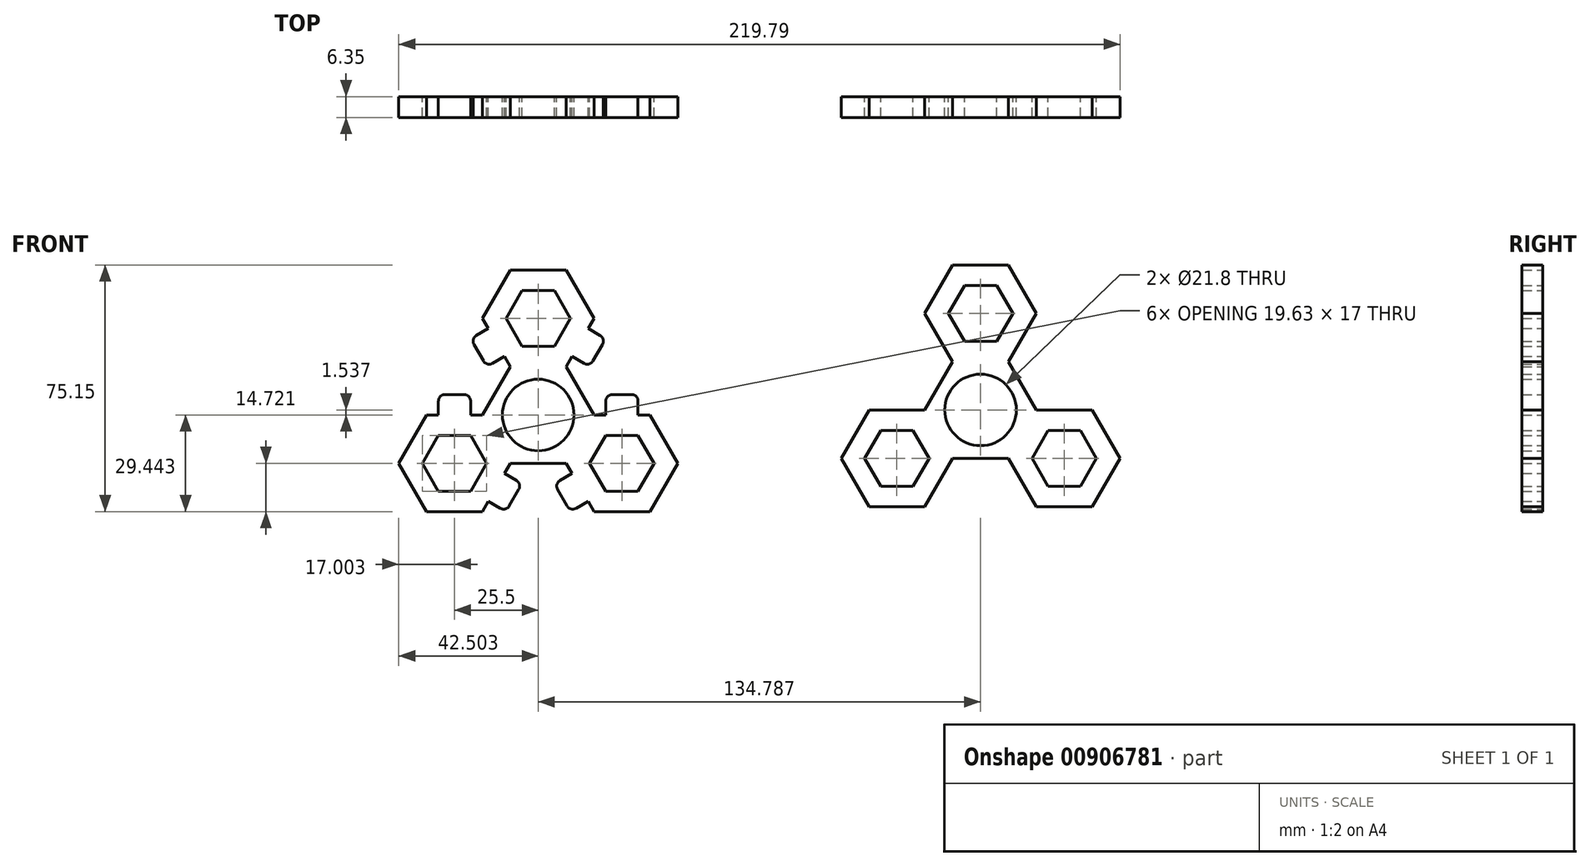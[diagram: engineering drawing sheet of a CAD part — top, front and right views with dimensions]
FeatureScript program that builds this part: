
annotation { "Feature Type Name" : "Feature", "Feature Type Description" : "" }
export const myFeature = defineFeature(function(context is Context, id is Id, definition is map)
    precondition{}
    {
        {
            var Q0;
            Q0=qCreatedBy(makeId("Front.planeOp"),FACE);
            var sketch = newSketch(context, id + "F0", { "sketchPlane" : qUnion([Q0])});
            skCircle(sketch, "E0", {"center": v(0, 0) * mm, "radius": 10.9 * mm});
            skCircle(sketch, "E1.cCircle", {"center": v(0, 0) * mm, "radius": 14.72 * mm, "construction": true});
            skLineSegment(sketch, "E1.0", {"start": v(8.5, 14.72) * mm, "end": v(17, 0) * mm});
            skLineSegment(sketch, "E1.2", {"start": v(8.5, -14.72) * mm, "end": v(-8.5, -14.72) * mm});
            skLineSegment(sketch, "E1.4", {"start": v(-17, 0) * mm, "end": v(-8.5, 14.72) * mm});
            skPoint(sketch, "E1.0.midPoint", {"position": v(12.75, 7.36) * mm});
            skCircle(sketch, "E2.cCircle", {"center": v(0, 29.44) * mm, "radius": 14.72 * mm, "construction": true});
            skLineSegment(sketch, "E2.1", {"start": v(-8.5, 14.72) * mm, "end": v(-17, 29.44) * mm});
            skLineSegment(sketch, "E2.2", {"start": v(-17, 29.44) * mm, "end": v(-8.5, 44.17) * mm});
            skLineSegment(sketch, "E2.3", {"start": v(-8.5, 44.17) * mm, "end": v(8.5, 44.17) * mm});
            skLineSegment(sketch, "E2.4", {"start": v(8.5, 44.17) * mm, "end": v(17, 29.44) * mm});
            skLineSegment(sketch, "E2.5", {"start": v(17, 29.44) * mm, "end": v(8.5, 14.72) * mm});
            skPoint(sketch, "E2.0.midPoint", {"position": v(0, 14.72) * mm});
            skLineSegment(sketch, "E3.1.0", {"start": v(-8.5, -14.72) * mm, "end": v(-17, -29.44) * mm});
            skLineSegment(sketch, "E3.1.1", {"start": v(-17, -29.44) * mm, "end": v(-34, -29.44) * mm});
            skLineSegment(sketch, "E3.1.2", {"start": v(-34, -29.44) * mm, "end": v(-42.5, -14.72) * mm});
            skLineSegment(sketch, "E3.1.3", {"start": v(-42.5, -14.72) * mm, "end": v(-34, 0) * mm});
            skLineSegment(sketch, "E3.1.4", {"start": v(-34, 0) * mm, "end": v(-17, 0) * mm});
            skCircle(sketch, "E3.1.5", {"center": v(-25.5, -14.72) * mm, "radius": 14.72 * mm, "construction": true});
            skLineSegment(sketch, "E3.2.0", {"start": v(17, 0) * mm, "end": v(34, 0) * mm});
            skLineSegment(sketch, "E3.2.1", {"start": v(34, 0) * mm, "end": v(42.5, -14.72) * mm});
            skLineSegment(sketch, "E3.2.2", {"start": v(42.5, -14.72) * mm, "end": v(34, -29.44) * mm});
            skLineSegment(sketch, "E3.2.3", {"start": v(34, -29.44) * mm, "end": v(17, -29.44) * mm});
            skLineSegment(sketch, "E3.2.4", {"start": v(17, -29.44) * mm, "end": v(8.5, -14.72) * mm});
            skCircle(sketch, "E3.2.5", {"center": v(25.5, -14.72) * mm, "radius": 14.72 * mm, "construction": true});
            skCircle(sketch, "E4.cCircle", {"center": v(-25.5, -14.72) * mm, "radius": 8.5 * mm, "construction": true});
            skLineSegment(sketch, "E4.0", {"start": v(-20.6, -23.22) * mm, "end": v(-30.4, -23.22) * mm});
            skLineSegment(sketch, "E4.1", {"start": v(-30.4, -23.22) * mm, "end": v(-35.31, -14.72) * mm});
            skLineSegment(sketch, "E4.2", {"start": v(-35.31, -14.72) * mm, "end": v(-30.4, -6.22) * mm});
            skLineSegment(sketch, "E4.3", {"start": v(-30.4, -6.22) * mm, "end": v(-20.6, -6.22) * mm});
            skLineSegment(sketch, "E4.4", {"start": v(-20.6, -6.22) * mm, "end": v(-15.69, -14.72) * mm});
            skLineSegment(sketch, "E4.5", {"start": v(-15.69, -14.72) * mm, "end": v(-20.6, -23.22) * mm});
            skPoint(sketch, "E4.0.midPoint", {"position": v(-25.5, -23.22) * mm});
            skLineSegment(sketch, "E5.1.0", {"start": v(20.6, -6.22) * mm, "end": v(30.4, -6.22) * mm});
            skLineSegment(sketch, "E5.1.1", {"start": v(15.69, -14.72) * mm, "end": v(20.6, -6.22) * mm});
            skLineSegment(sketch, "E5.1.2", {"start": v(35.31, -14.72) * mm, "end": v(30.4, -23.22) * mm});
            skPoint(sketch, "E5.1.3", {"position": v(32.86, -10.47) * mm});
            skLineSegment(sketch, "E5.1.4", {"start": v(30.4, -6.22) * mm, "end": v(35.31, -14.72) * mm});
            skLineSegment(sketch, "E5.1.5", {"start": v(30.4, -23.22) * mm, "end": v(20.6, -23.22) * mm});
            skCircle(sketch, "E5.1.6", {"center": v(25.5, -14.72) * mm, "radius": 8.5 * mm, "construction": true});
            skLineSegment(sketch, "E5.1.7", {"start": v(20.6, -23.22) * mm, "end": v(15.69, -14.72) * mm});
            skLineSegment(sketch, "E5.2.0", {"start": v(-4.9, 20.94) * mm, "end": v(-9.81, 29.44) * mm});
            skLineSegment(sketch, "E5.2.1", {"start": v(4.9, 20.94) * mm, "end": v(-4.9, 20.94) * mm});
            skLineSegment(sketch, "E5.2.2", {"start": v(-4.9, 37.94) * mm, "end": v(4.9, 37.94) * mm});
            skPoint(sketch, "E5.2.3", {"position": v(-7.36, 33.7) * mm});
            skLineSegment(sketch, "E5.2.4", {"start": v(-9.81, 29.44) * mm, "end": v(-4.9, 37.94) * mm});
            skLineSegment(sketch, "E5.2.5", {"start": v(4.9, 37.94) * mm, "end": v(9.81, 29.44) * mm});
            skCircle(sketch, "E5.2.6", {"center": v(0, 29.44) * mm, "radius": 8.5 * mm, "construction": true});
            skLineSegment(sketch, "E5.2.7", {"start": v(9.81, 29.44) * mm, "end": v(4.9, 20.94) * mm});
            skCircle(sketch, "E6", {"center": v(-134.79, -1.54) * mm, "radius": 10.9 * mm});
            skLineSegment(sketch, "E7.0", {"start": v(-126.29, 13.19) * mm, "end": v(-117.79, -1.54) * mm});
            skLineSegment(sketch, "E7.2", {"start": v(-126.29, -16.26) * mm, "end": v(-143.29, -16.26) * mm});
            skLineSegment(sketch, "E7.4", {"start": v(-151.79, -1.54) * mm, "end": v(-143.29, 13.19) * mm});
            skPoint(sketch, "E7.0.midPoint", {"position": v(-122.04, 5.82) * mm});
            skLineSegment(sketch, "E8.1", {"start": v(-143.29, 13.19) * mm, "end": v(-145.08, 16.3) * mm});
            skLineSegment(sketch, "E8.2", {"start": v(-151.79, 27.9) * mm, "end": v(-143.29, 42.63) * mm});
            skLineSegment(sketch, "E8.3", {"start": v(-143.29, 42.63) * mm, "end": v(-126.29, 42.63) * mm});
            skLineSegment(sketch, "E8.5", {"start": v(-117.79, 27.9) * mm, "end": v(-119.58, 24.8) * mm});
            skPoint(sketch, "E8.0.midPoint", {"position": v(-134.79, 13.19) * mm});
            skLineSegment(sketch, "E9.1.0", {"start": v(-143.29, -16.26) * mm, "end": v(-145.08, -19.37) * mm});
            skLineSegment(sketch, "E9.1.1", {"start": v(-151.79, -30.98) * mm, "end": v(-168.79, -30.98) * mm});
            skLineSegment(sketch, "E9.1.2", {"start": v(-168.79, -30.98) * mm, "end": v(-177.29, -16.26) * mm});
            skLineSegment(sketch, "E9.1.3", {"start": v(-177.29, -16.26) * mm, "end": v(-168.79, -1.54) * mm});
            skLineSegment(sketch, "E9.1.4", {"start": v(-168.79, -1.54) * mm, "end": v(-165.2, -1.54) * mm});
            skLineSegment(sketch, "E9.2.0", {"start": v(-117.79, -1.54) * mm, "end": v(-114.2, -1.54) * mm});
            skLineSegment(sketch, "E9.2.1", {"start": v(-100.79, -1.54) * mm, "end": v(-92.29, -16.26) * mm});
            skLineSegment(sketch, "E9.2.2", {"start": v(-92.29, -16.26) * mm, "end": v(-100.79, -30.98) * mm});
            skLineSegment(sketch, "E9.2.3", {"start": v(-100.79, -30.98) * mm, "end": v(-117.79, -30.98) * mm});
            skLineSegment(sketch, "E9.2.4", {"start": v(-117.79, -30.98) * mm, "end": v(-119.58, -27.87) * mm});
            skCircle(sketch, "E10.cCircle", {"center": v(-160.29, -16.26) * mm, "radius": 8.5 * mm, "construction": true});
            skLineSegment(sketch, "E10.0", {"start": v(-155.38, -24.76) * mm, "end": v(-165.2, -24.76) * mm});
            skLineSegment(sketch, "E10.1", {"start": v(-165.2, -24.76) * mm, "end": v(-170.1, -16.26) * mm});
            skLineSegment(sketch, "E10.2", {"start": v(-170.1, -16.26) * mm, "end": v(-165.2, -7.76) * mm});
            skLineSegment(sketch, "E10.3", {"start": v(-165.2, -7.76) * mm, "end": v(-155.38, -7.76) * mm});
            skLineSegment(sketch, "E10.4", {"start": v(-155.38, -7.76) * mm, "end": v(-150.47, -16.26) * mm});
            skLineSegment(sketch, "E10.5", {"start": v(-150.47, -16.26) * mm, "end": v(-155.38, -24.76) * mm});
            skPoint(sketch, "E10.0.midPoint", {"position": v(-160.29, -24.76) * mm});
            skLineSegment(sketch, "E11.1.0", {"start": v(-114.2, -7.76) * mm, "end": v(-104.38, -7.76) * mm});
            skLineSegment(sketch, "E11.1.1", {"start": v(-119.1, -16.26) * mm, "end": v(-114.2, -7.76) * mm});
            skLineSegment(sketch, "E11.1.2", {"start": v(-99.47, -16.26) * mm, "end": v(-104.38, -24.76) * mm});
            skPoint(sketch, "E11.1.3", {"position": v(-101.93, -12) * mm});
            skLineSegment(sketch, "E11.1.4", {"start": v(-104.38, -7.76) * mm, "end": v(-99.47, -16.26) * mm});
            skLineSegment(sketch, "E11.1.5", {"start": v(-104.38, -24.76) * mm, "end": v(-114.2, -24.76) * mm});
            skCircle(sketch, "E11.1.6", {"center": v(-109.29, -16.26) * mm, "radius": 8.5 * mm, "construction": true});
            skLineSegment(sketch, "E11.1.7", {"start": v(-114.2, -24.76) * mm, "end": v(-119.1, -16.26) * mm});
            skLineSegment(sketch, "E11.2.0", {"start": v(-139.7, 19.4) * mm, "end": v(-144.6, 27.9) * mm});
            skLineSegment(sketch, "E11.2.1", {"start": v(-129.88, 19.4) * mm, "end": v(-139.7, 19.4) * mm});
            skLineSegment(sketch, "E11.2.2", {"start": v(-139.7, 36.4) * mm, "end": v(-129.88, 36.4) * mm});
            skPoint(sketch, "E11.2.3", {"position": v(-142.15, 32.16) * mm});
            skLineSegment(sketch, "E11.2.4", {"start": v(-144.6, 27.9) * mm, "end": v(-139.7, 36.4) * mm});
            skLineSegment(sketch, "E11.2.5", {"start": v(-129.88, 36.4) * mm, "end": v(-124.97, 27.9) * mm});
            skCircle(sketch, "E11.2.6", {"center": v(-134.79, 27.9) * mm, "radius": 8.5 * mm, "construction": true});
            skLineSegment(sketch, "E11.2.7", {"start": v(-124.97, 27.9) * mm, "end": v(-129.88, 19.4) * mm});
            skLineSegment(sketch, "E12", {"start": v(-126.29, 42.63) * mm, "end": v(-117.79, 27.9) * mm});
            skLineSegment(sketch, "E13", {"start": v(-120.31, 25.22) * mm, "end": v(-115.93, 22.69) * mm});
            skLineSegment(sketch, "E14", {"start": v(-125.22, 16.72) * mm, "end": v(-120.83, 14.19) * mm});
            skLineSegment(sketch, "E15.trimOffspring", {"start": v(-124.5, 16.3) * mm, "end": v(-126.29, 13.19) * mm});
            skLineSegment(sketch, "E16", {"start": v(-115.2, 19.95) * mm, "end": v(-118.1, 14.92) * mm});
            skLineSegment(sketch, "E17.MirrorCS", {"start": v(-149.26, 25.22) * mm, "end": v(-153.65, 22.69) * mm});
            skLineSegment(sketch, "E18.MirrorCS", {"start": v(-154.38, 19.95) * mm, "end": v(-151.47, 14.92) * mm});
            skLineSegment(sketch, "E19.MirrorCS", {"start": v(-144.35, 16.72) * mm, "end": v(-148.74, 14.19) * mm});
            skLineSegment(sketch, "E20.MirrorCS", {"start": v(-143.6, -29.25) * mm, "end": v(-140.7, -24.21) * mm});
            skLineSegment(sketch, "E21.MirrorCS", {"start": v(-145.81, -18.95) * mm, "end": v(-141.43, -21.48) * mm});
            skLineSegment(sketch, "E22.MirrorCS", {"start": v(-150.72, -27.45) * mm, "end": v(-146.33, -29.98) * mm});
            skLineSegment(sketch, "E23.MirrorCS", {"start": v(-163.2, 4.69) * mm, "end": v(-157.38, 4.69) * mm});
            skLineSegment(sketch, "E24.MirrorCS", {"start": v(-165.2, -2.38) * mm, "end": v(-165.2, 2.69) * mm});
            skLineSegment(sketch, "E25.MirrorCS", {"start": v(-155.38, -2.38) * mm, "end": v(-155.38, 2.69) * mm});
            skLineSegment(sketch, "E26.MirrorCS", {"start": v(-106.38, 4.69) * mm, "end": v(-112.2, 4.69) * mm});
            skLineSegment(sketch, "E27.MirrorCS", {"start": v(-104.38, -2.38) * mm, "end": v(-104.38, 2.69) * mm});
            skLineSegment(sketch, "E28.MirrorCS", {"start": v(-114.2, -2.38) * mm, "end": v(-114.2, 2.69) * mm});
            skLineSegment(sketch, "E29.MirrorCS", {"start": v(-125.97, -29.25) * mm, "end": v(-128.88, -24.21) * mm});
            skLineSegment(sketch, "E30.MirrorCS", {"start": v(-118.85, -27.45) * mm, "end": v(-123.24, -29.98) * mm});
            skLineSegment(sketch, "E31.MirrorCS", {"start": v(-123.76, -18.95) * mm, "end": v(-128.15, -21.48) * mm});
            skLineSegment(sketch, "E32.trimOffspring", {"start": v(-104.38, -1.54) * mm, "end": v(-100.79, -1.54) * mm});
            skLineSegment(sketch, "E33.trimOffspring", {"start": v(-150, 24.8) * mm, "end": v(-151.79, 27.9) * mm});
            skLineSegment(sketch, "E34.trimOffspring", {"start": v(-155.38, -1.54) * mm, "end": v(-151.79, -1.54) * mm});
            skLineSegment(sketch, "E35.trimOffspring", {"start": v(-150, -27.87) * mm, "end": v(-151.79, -30.98) * mm});
            skLineSegment(sketch, "E36.trimOffspring", {"start": v(-124.5, -19.37) * mm, "end": v(-126.29, -16.26) * mm});
            skPoint(sketch, "E37.orphan", {"position": v(-119.1, -16.26) * mm});
            skPoint(sketch, "E38.orphan", {"position": v(-114.2, -24.76) * mm});
            skPoint(sketch, "E39.orphan", {"position": v(-114.2, -7.76) * mm});
            skPoint(sketch, "E40.orphan", {"position": v(-104.38, -7.76) * mm});
            skPoint(sketch, "E41.orphan", {"position": v(-139.7, 19.4) * mm});
            skPoint(sketch, "E42.orphan", {"position": v(-144.6, 27.9) * mm});
            skPoint(sketch, "E43.orphan", {"position": v(-165.2, -7.76) * mm});
            skPoint(sketch, "E44.orphan", {"position": v(-155.38, -7.76) * mm});
            skPoint(sketch, "E45.orphan", {"position": v(-150.47, -16.26) * mm});
            skPoint(sketch, "E46.orphan", {"position": v(-155.38, -24.76) * mm});
            skPoint(sketch, "E47.visualSharp", {"position": v(-114.2, 21.69) * mm});
            skArc(sketch, "E47.filletArc", {"start": v(-115.2, 19.95) * mm, "mid": v(-115, 21.47) * mm, "end": v(-115.93, 22.69) * mm});
            skPoint(sketch, "E48.visualSharp", {"position": v(-119.1, 13.19) * mm});
            skArc(sketch, "E48.filletArc", {"start": v(-120.83, 14.19) * mm, "mid": v(-119.32, 13.99) * mm, "end": v(-118.1, 14.92) * mm});
            skPoint(sketch, "E49.visualSharp", {"position": v(-150.47, 13.19) * mm});
            skArc(sketch, "E49.filletArc", {"start": v(-151.47, 14.92) * mm, "mid": v(-150.26, 13.99) * mm, "end": v(-148.74, 14.19) * mm});
            skPoint(sketch, "E50.visualSharp", {"position": v(-155.38, 21.69) * mm});
            skArc(sketch, "E50.filletArc", {"start": v(-153.65, 22.69) * mm, "mid": v(-154.58, 21.47) * mm, "end": v(-154.38, 19.95) * mm});
            skPoint(sketch, "E51.visualSharp", {"position": v(-155.38, 4.69) * mm});
            skArc(sketch, "E51.filletArc", {"start": v(-155.38, 2.69) * mm, "mid": v(-155.97, 4.1) * mm, "end": v(-157.38, 4.69) * mm});
            skPoint(sketch, "E52.visualSharp", {"position": v(-144.6, -30.98) * mm});
            skArc(sketch, "E52.filletArc", {"start": v(-146.33, -29.98) * mm, "mid": v(-144.82, -30.18) * mm, "end": v(-143.6, -29.25) * mm});
            skPoint(sketch, "E53.visualSharp", {"position": v(-165.2, 4.69) * mm});
            skArc(sketch, "E53.filletArc", {"start": v(-163.2, 4.69) * mm, "mid": v(-164.6, 4.1) * mm, "end": v(-165.2, 2.69) * mm});
            skPoint(sketch, "E54.visualSharp", {"position": v(-139.7, -22.48) * mm});
            skArc(sketch, "E54.filletArc", {"start": v(-140.7, -24.21) * mm, "mid": v(-140.5, -22.7) * mm, "end": v(-141.43, -21.48) * mm});
            skPoint(sketch, "E55.visualSharp", {"position": v(-129.88, -22.48) * mm});
            skArc(sketch, "E55.filletArc", {"start": v(-128.15, -21.48) * mm, "mid": v(-129.08, -22.7) * mm, "end": v(-128.88, -24.21) * mm});
            skPoint(sketch, "E56.visualSharp", {"position": v(-124.97, -30.98) * mm});
            skArc(sketch, "E56.filletArc", {"start": v(-125.97, -29.25) * mm, "mid": v(-124.76, -30.18) * mm, "end": v(-123.24, -29.98) * mm});
            skPoint(sketch, "E57.visualSharp", {"position": v(-114.2, 4.69) * mm});
            skArc(sketch, "E57.filletArc", {"start": v(-112.2, 4.69) * mm, "mid": v(-113.6, 4.1) * mm, "end": v(-114.2, 2.69) * mm});
            skPoint(sketch, "E58.visualSharp", {"position": v(-104.38, 4.69) * mm});
            skArc(sketch, "E58.filletArc", {"start": v(-104.38, 2.69) * mm, "mid": v(-104.97, 4.1) * mm, "end": v(-106.38, 4.69) * mm});
            skSolve(sketch);
        }
        {
            var Q0;
            Q0=makeQuery(id+"F0.imprint","IMPRINT",FACE,{"disambiguationData":[TD([[makeQuery(id+"F0.imprint","IMPRINT",EDGE,{"derivedFrom":sQuery(id+"F0.wireOp",EDGE,"E0")}),-1.0]])]});
            extrude(context, id + "F1", {"entities" : qUnion([Q0]), "depth" : 6.35 * mm, "offsetDistance" : 25 * mm});
        }
        {
            var Q0;
            Q0 = qSketchRegion(id + "F0", true);
            extrude(context, id + "F2", {"entities" : qUnion([Q0]), "operationType" : NewBodyOperationType.ADD, "depth" : 6.35 * mm, "offsetDistance" : 25 * mm});
        }
    });
